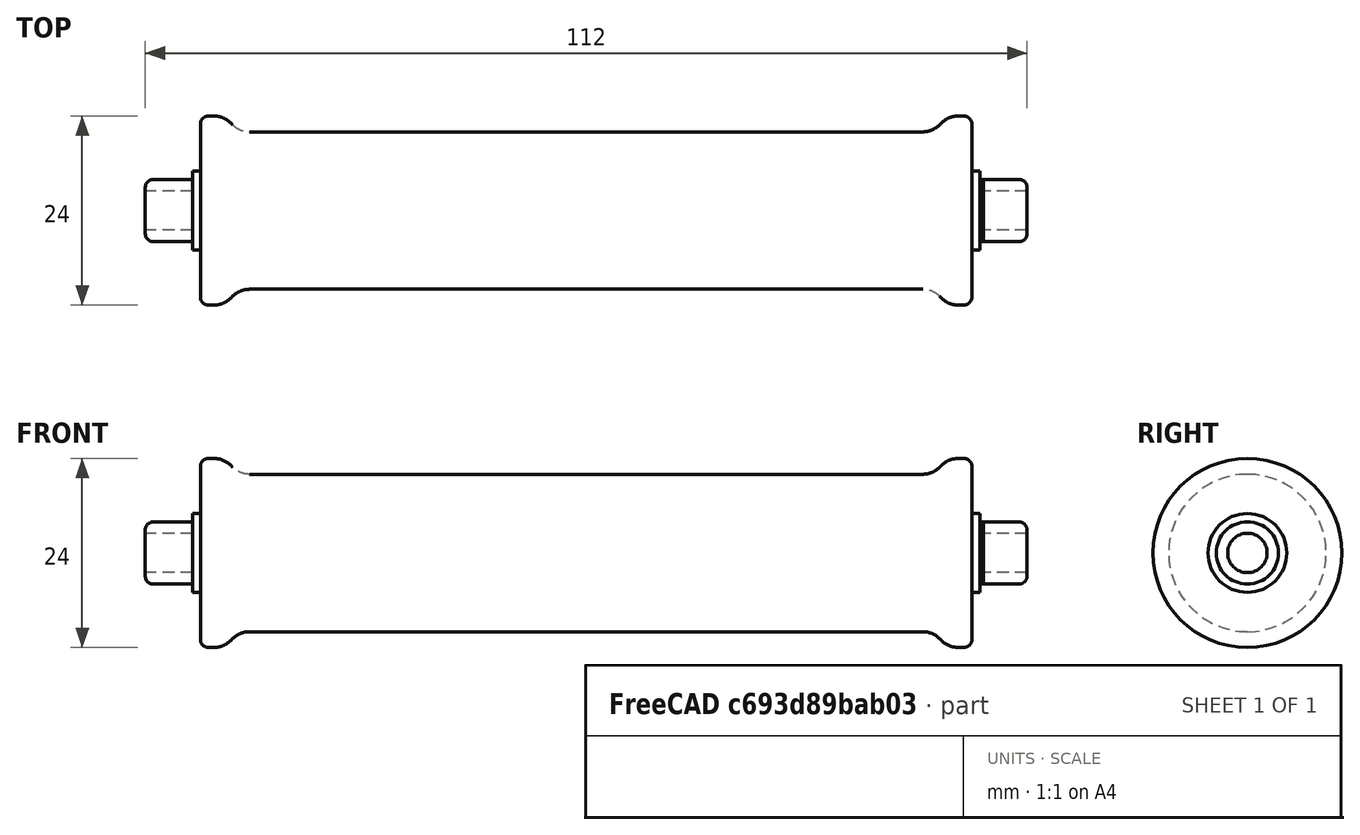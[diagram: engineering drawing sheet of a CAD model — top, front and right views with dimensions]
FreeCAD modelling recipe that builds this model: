
FCSTD DOCUMENT  (FreeCAD 0.18R16146 (Git))
Label: FillerRollerSource
License: All rights reserved
LicenseURL: http://en.wikipedia.org/wiki/All_rights_reserved
objects: Part::Cut×4, Part::Feature×3, Part::Cylinder×2, PartDesign::FeatureBase×1, PartDesign::Body×1
note: 11 computed .brp shape members not serialized (recipe doc carries the construction recipe); baked Part::Feature solids carry a one-line shape summary decoded from their .brp

FEATURE [Part::Feature] Part__Feature  label="FilamentHolder3dpnFinal v22"
  shape: bbox 112 x 25.98 x 25.98 mm, 23 faces (baked)
FEATURE [Part::Feature] Part__Feature_cs
  shape: bbox 112 x 24 x 3e-07 mm, 0 faces, 0 solids (baked)
FEATURE [PartDesign::FeatureBase] BaseFeature
  BaseFeature = -> Part__Feature
FEATURE [PartDesign::Body] Body
  BaseFeature = -> Part__Feature
  Group = -> [BaseFeature]
  Origin = -> Origin
  Tip = -> BaseFeature
FEATURE [Part::Feature] BaseFeature001
  shape: bbox 112 x 25.98 x 25.98 mm, 23 faces (baked)
FEATURE [Part::Cylinder] Cylinder
  Angle = 360
  AttacherType = Attacher::AttachEngine3D
  Height = 10
  Radius = 5
FEATURE [Part::Cylinder] Cylinder001
  Angle = 360
  AttacherType = Attacher::AttachEngine3D
  Height = 10
  Radius = 2.5
FEATURE [Part::Cut] Cut
  Base = -> Cylinder
  Placement = pos=(129,0,35) rot=(0,1,0;4.71239rad)
  Tool = -> Cylinder001
FEATURE [Part::Cut] Cut001
  Base = -> Cylinder
  Placement = pos=(18.5,0,35) rot=(0,-1,0;1.5708rad)
  Tool = -> Cylinder001
FEATURE [Part::Cut] Cut002
  Base = -> BaseFeature001
  Tool = -> Cut
FEATURE [Part::Cut] Cut003
  Base = -> Cut002
  Tool = -> Cut001
